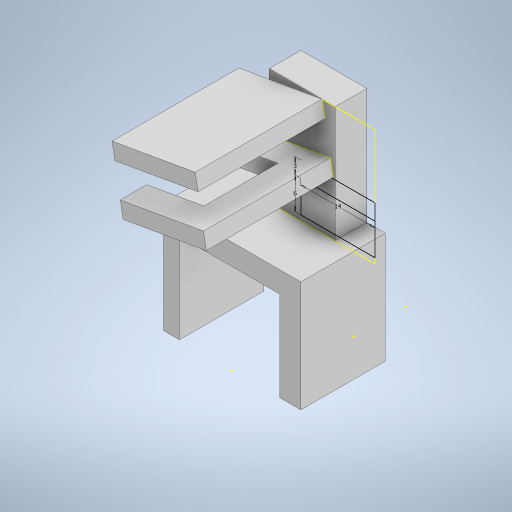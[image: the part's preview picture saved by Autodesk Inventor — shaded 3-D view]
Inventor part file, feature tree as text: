
AUTODESK INVENTOR PART (.ipt)
format: ipt  version: 2023 (Build 270158000, 158)  size: 751,616 bytes
history: native  units: mm
features: sketch x16, projected_geometry x14, extrude x12
ambient origin geometry x8: Origin, YZ Plane, XZ Plane, XY Plane, X Axis, Y Axis, Z Axis, Center Point
bodies: Solid1 (feature_tree)
feature tree (42):
  extrude  "Extrusion1"  Depth=33.0mm
  extrude  "Extrusion2"  Depth=4.0mm
  extrude  "Extrusion3"  Depth=17.0mm TaperAngle=0.0deg
  sketch  "Sketch4"  dims[d8=6.0mm d9=6.0mm]
  extrude  "Extrusion4"  Depth=6.0mm
  extrude  "Extrusion5"  Depth=14.0mm
  extrude  "Extrusion6"  Depth=6.0mm
  sketch  "Sketch8"  dims[d18=29.670597mm d19=3.0mm]
  sketch  "Sketch9"  dims[d20=6.0mm d21=3.0mm]
  sketch  "Sketch10"  dims[d22=16.0mm d23=24.0mm d24=0.0mm]
  sketch  "Sketch11"  dims[d25=17.0mm d26=0.0mm d27=16.0mm]
  sketch  "Sketch12"  dims[d28=29.670597mm d29=16.0mm]
  extrude  "Extrusion7"  Depth=16.0mm
  extrude  "Extrusion8"  Depth=3.0mm
  extrude  "Extrusion9"  Depth=3.0mm
  extrude  "Extrusion10"  Depth=24.0mm TaperAngle=0.0deg
  sketch  "Sketch13"  dims[d30=6.0mm]
  extrude  "Extrusion11"  Depth=16.0mm
  sketch  "Sketch16"  dims[d32=3.0mm]
  extrude  "Extrusion12"  Depth=16.0mm
  sketch  "Sketch1"  dims[d0=26.0mm d1=33.0mm]
  sketch  "Sketch2"  dims[d2=4.0mm d3=0.0mm d4=4.0mm]
  projected_geometry  "Projected Loop1"
  sketch  "Sketch3"  dims[d5=3.0mm d6=17.0mm d7=0.0mm]
  projected_geometry  "Projected Loop2"
  projected_geometry  "Projected Loop3"
  sketch  "Sketch5"  dims[d10=10.0mm d11=0.0mm d12=14.0mm]
  projected_geometry  "Projected Loop4"
  sketch  "Sketch6"  dims[d13=3.0mm d14=6.0mm]
  sketch  "Sketch7"  dims[d15=12.0mm d16=0.0mm d17=16.0mm]
  projected_geometry  "Projected Loop5"
  projected_geometry  "Projected Loop6"
  projected_geometry  "Projected Loop7"
  projected_geometry  "Projected Loop8"
  projected_geometry  "Projected Loop9"
  projected_geometry  "Projected Loop10"
  projected_geometry  "Projected Loop11"
  projected_geometry  "Projected Loop12"
  sketch  "Sketch15"  dims[d31=13.962634mm]
  projected_geometry  "Projected Loop13"
  sketch  "Sketch17"  dims[d33=13.962634mm d34=16.0mm d35=10.0mm d36=0.0mm d37=10.0mm d38=0.0mm d39=10.0mm d40=0.0mm d41=10.0mm d42=0.0mm d43=5.0mm d44=5.0mm d45=90.0deg d46=11.0mm d47=4.0mm d48=0.0mm d49=7.5mm d50=0.0mm]
  projected_geometry  "Projected Loop14"
